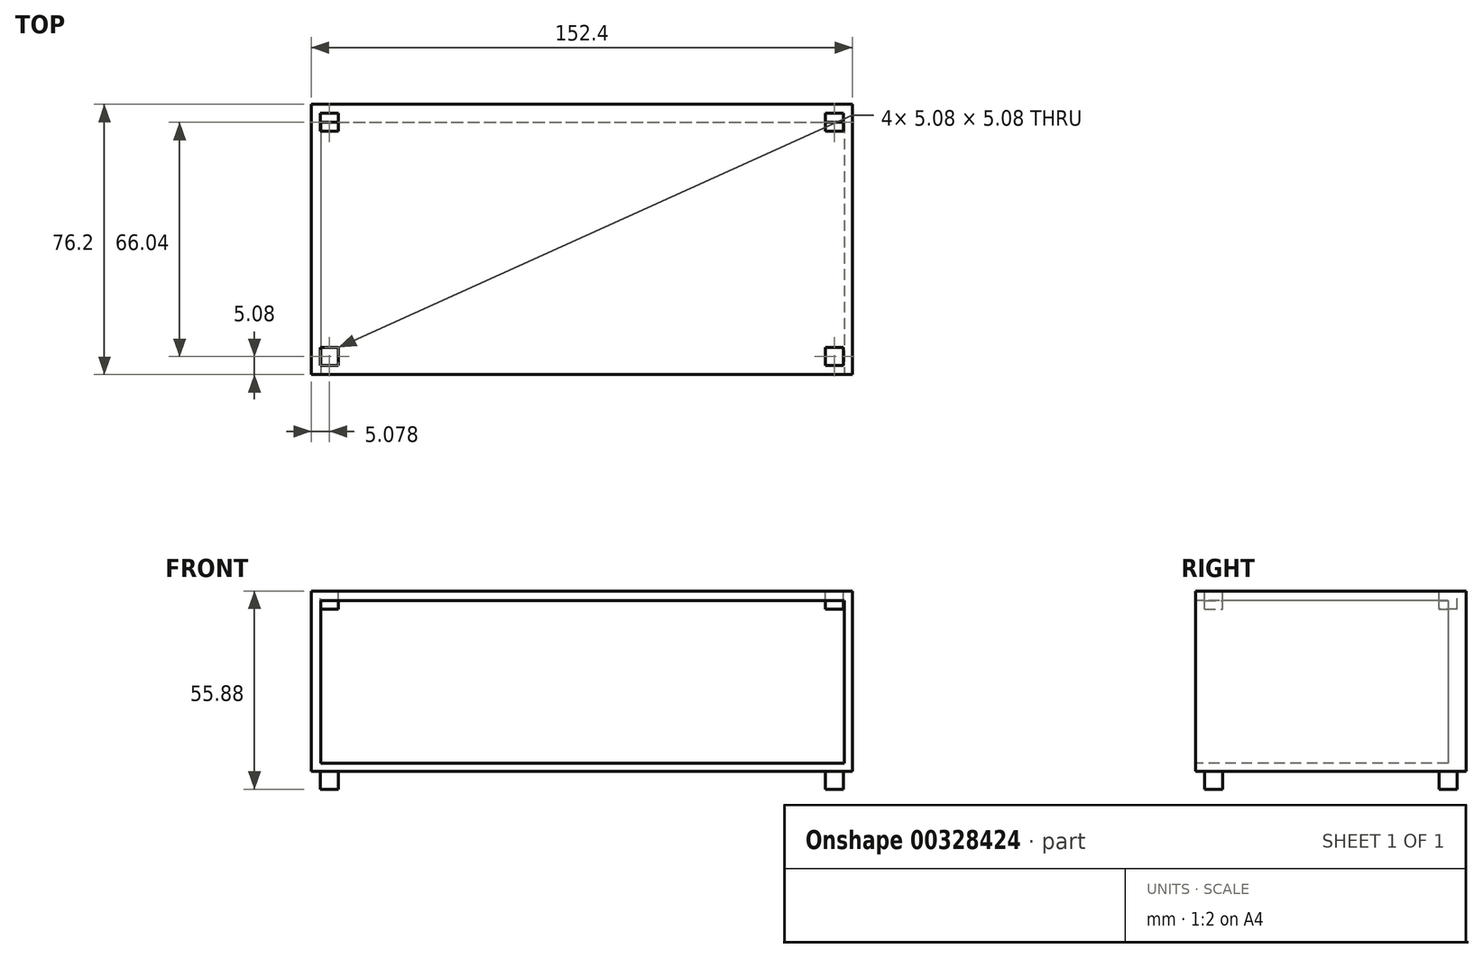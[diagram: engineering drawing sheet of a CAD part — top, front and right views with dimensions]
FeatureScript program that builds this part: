
annotation { "Feature Type Name" : "Feature", "Feature Type Description" : "" }
export const myFeature = defineFeature(function(context is Context, id is Id, definition is map)
    precondition{}
    {
        {
            var Q0;
            Q0=qCreatedBy(makeId("Front.planeOp"),FACE);
            var sketch = newSketch(context, id + "F0", { "sketchPlane" : qUnion([Q0])});
            skLineSegment(sketch, "E0.bottom", {"start": v(-70.66, 22.12) * mm, "end": v(81.74, 22.12) * mm});
            skLineSegment(sketch, "E0.top", {"start": v(-70.66, -28.68) * mm, "end": v(81.74, -28.68) * mm});
            skLineSegment(sketch, "E0.left", {"start": v(-70.66, 22.12) * mm, "end": v(-70.66, -28.68) * mm});
            skLineSegment(sketch, "E0.right", {"start": v(81.74, 22.12) * mm, "end": v(81.74, -28.68) * mm});
            skSolve(sketch);
        }
        {
            var Q0;
            Q0=makeQuery(id+"F0.imprint","IMPRINT",FACE,{"disambiguationData":[TD([[makeQuery(id+"F0.imprint","IMPRINT",EDGE,{"derivedFrom":sQuery(id+"F0.wireOp",EDGE,"E0.bottom")}),-1.0]])]});
            extrude(context, id + "F1", {"entities" : qUnion([Q0]), "oppositeDirection" : true, "depth" : 76.2 * mm});
        }
        {
            var Q0;
            Q0=qCreatedBy(makeId("Front.planeOp"),FACE);
            var sketch = newSketch(context, id + "F2", { "sketchPlane" : qUnion([Q0])});
            skLineSegment(sketch, "E1.bottom", {"start": v(-68.06, 19.38) * mm, "end": v(79.43, 19.38) * mm});
            skLineSegment(sketch, "E1.top", {"start": v(-68.06, -26.38) * mm, "end": v(79.43, -26.38) * mm});
            skLineSegment(sketch, "E1.left", {"start": v(-68.06, 19.38) * mm, "end": v(-68.06, -26.38) * mm});
            skLineSegment(sketch, "E1.right", {"start": v(79.43, 19.38) * mm, "end": v(79.43, -26.38) * mm});
            skSolve(sketch);
        }
        {
            var Q0;
            Q0 = qSketchRegion(id + "F2", true);
            extrude(context, id + "F3", {"entities" : qUnion([Q0]), "operationType" : NewBodyOperationType.REMOVE, "oppositeDirection" : true, "depth" : 71.12 * mm});
        }
        {
            var Q0;
            Q0=makeQuery(id+"F1.opExtrude","SWEPT_FACE",FACE,{"disambiguationData":[OSD([sQuery(id+"F0.wireOp",EDGE,"E0.top")])]});
            var sketch = newSketch(context, id + "F4", { "sketchPlane" : qUnion([Q0])});
            skLineSegment(sketch, "E2.bottom", {"start": v(-68.12, -2.54) * mm, "end": v(-63.04, -2.54) * mm});
            skLineSegment(sketch, "E2.top", {"start": v(-68.12, -7.62) * mm, "end": v(-63.04, -7.62) * mm});
            skLineSegment(sketch, "E2.left", {"start": v(-68.12, -2.54) * mm, "end": v(-68.12, -7.62) * mm});
            skLineSegment(sketch, "E2.right", {"start": v(-63.04, -2.54) * mm, "end": v(-63.04, -7.62) * mm});
            skLineSegment(sketch, "E3.bottom", {"start": v(79.2, -2.54) * mm, "end": v(74.12, -2.54) * mm});
            skLineSegment(sketch, "E3.top", {"start": v(79.2, -7.62) * mm, "end": v(74.12, -7.62) * mm});
            skLineSegment(sketch, "E3.left", {"start": v(79.2, -2.54) * mm, "end": v(79.2, -7.62) * mm});
            skLineSegment(sketch, "E3.right", {"start": v(74.12, -2.54) * mm, "end": v(74.12, -7.62) * mm});
            skLineSegment(sketch, "E4.bottom", {"start": v(79.2, -73.66) * mm, "end": v(74.12, -73.66) * mm});
            skLineSegment(sketch, "E4.top", {"start": v(79.2, -68.58) * mm, "end": v(74.12, -68.58) * mm});
            skLineSegment(sketch, "E4.left", {"start": v(79.2, -73.66) * mm, "end": v(79.2, -68.58) * mm});
            skLineSegment(sketch, "E4.right", {"start": v(74.12, -73.66) * mm, "end": v(74.12, -68.58) * mm});
            skLineSegment(sketch, "E5.bottom", {"start": v(-63.04, -68.58) * mm, "end": v(-68.12, -68.58) * mm});
            skLineSegment(sketch, "E5.top", {"start": v(-63.04, -73.66) * mm, "end": v(-68.12, -73.66) * mm});
            skLineSegment(sketch, "E5.left", {"start": v(-63.04, -68.58) * mm, "end": v(-63.04, -73.66) * mm});
            skLineSegment(sketch, "E5.right", {"start": v(-68.12, -68.58) * mm, "end": v(-68.12, -73.66) * mm});
            skSolve(sketch);
        }
        {
            var Q0;
            Q0 = qSketchRegion(id + "F4", true);
            extrude(context, id + "F5", {"entities" : qUnion([Q0]), "operationType" : NewBodyOperationType.ADD, "depth" : 5.08 * mm});
        }
        {
            var Q0;
            Q0=makeQuery(id+"F1.opExtrude","SWEPT_FACE",FACE,{"disambiguationData":[OSD([sQuery(id+"F0.wireOp",EDGE,"E0.bottom")])]});
            var sketch = newSketch(context, id + "F6", { "sketchPlane" : qUnion([Q0])});
            skLineSegment(sketch, "E6.bottom", {"start": v(-68.12, 73.66) * mm, "end": v(-63.04, 73.66) * mm});
            skLineSegment(sketch, "E6.top", {"start": v(-68.12, 68.58) * mm, "end": v(-63.04, 68.58) * mm});
            skLineSegment(sketch, "E6.left", {"start": v(-68.12, 73.66) * mm, "end": v(-68.12, 68.58) * mm});
            skLineSegment(sketch, "E6.right", {"start": v(-63.04, 73.66) * mm, "end": v(-63.04, 68.58) * mm});
            skLineSegment(sketch, "E7.bottom", {"start": v(-68.12, 7.62) * mm, "end": v(-63.04, 7.62) * mm});
            skLineSegment(sketch, "E7.top", {"start": v(-68.12, 2.54) * mm, "end": v(-63.04, 2.54) * mm});
            skLineSegment(sketch, "E7.left", {"start": v(-68.12, 7.62) * mm, "end": v(-68.12, 2.54) * mm});
            skLineSegment(sketch, "E7.right", {"start": v(-63.04, 7.62) * mm, "end": v(-63.04, 2.54) * mm});
            skLineSegment(sketch, "E8.bottom", {"start": v(74.12, 73.66) * mm, "end": v(79.2, 73.66) * mm});
            skLineSegment(sketch, "E8.top", {"start": v(74.12, 68.58) * mm, "end": v(79.2, 68.58) * mm});
            skLineSegment(sketch, "E8.left", {"start": v(74.12, 73.66) * mm, "end": v(74.12, 68.58) * mm});
            skLineSegment(sketch, "E8.right", {"start": v(79.2, 73.66) * mm, "end": v(79.2, 68.58) * mm});
            skLineSegment(sketch, "E9.bottom", {"start": v(74.12, 7.62) * mm, "end": v(79.2, 7.62) * mm});
            skLineSegment(sketch, "E9.top", {"start": v(74.12, 2.54) * mm, "end": v(79.2, 2.54) * mm});
            skLineSegment(sketch, "E9.left", {"start": v(74.12, 7.62) * mm, "end": v(74.12, 2.54) * mm});
            skLineSegment(sketch, "E9.right", {"start": v(79.2, 7.62) * mm, "end": v(79.2, 2.54) * mm});
            skSolve(sketch);
        }
        {
            var Q0;
            Q0 = qSketchRegion(id + "F6", true);
            extrude(context, id + "F7", {"entities" : qUnion([Q0]), "operationType" : NewBodyOperationType.REMOVE, "oppositeDirection" : true, "depth" : 5.08 * mm});
        }
    });
